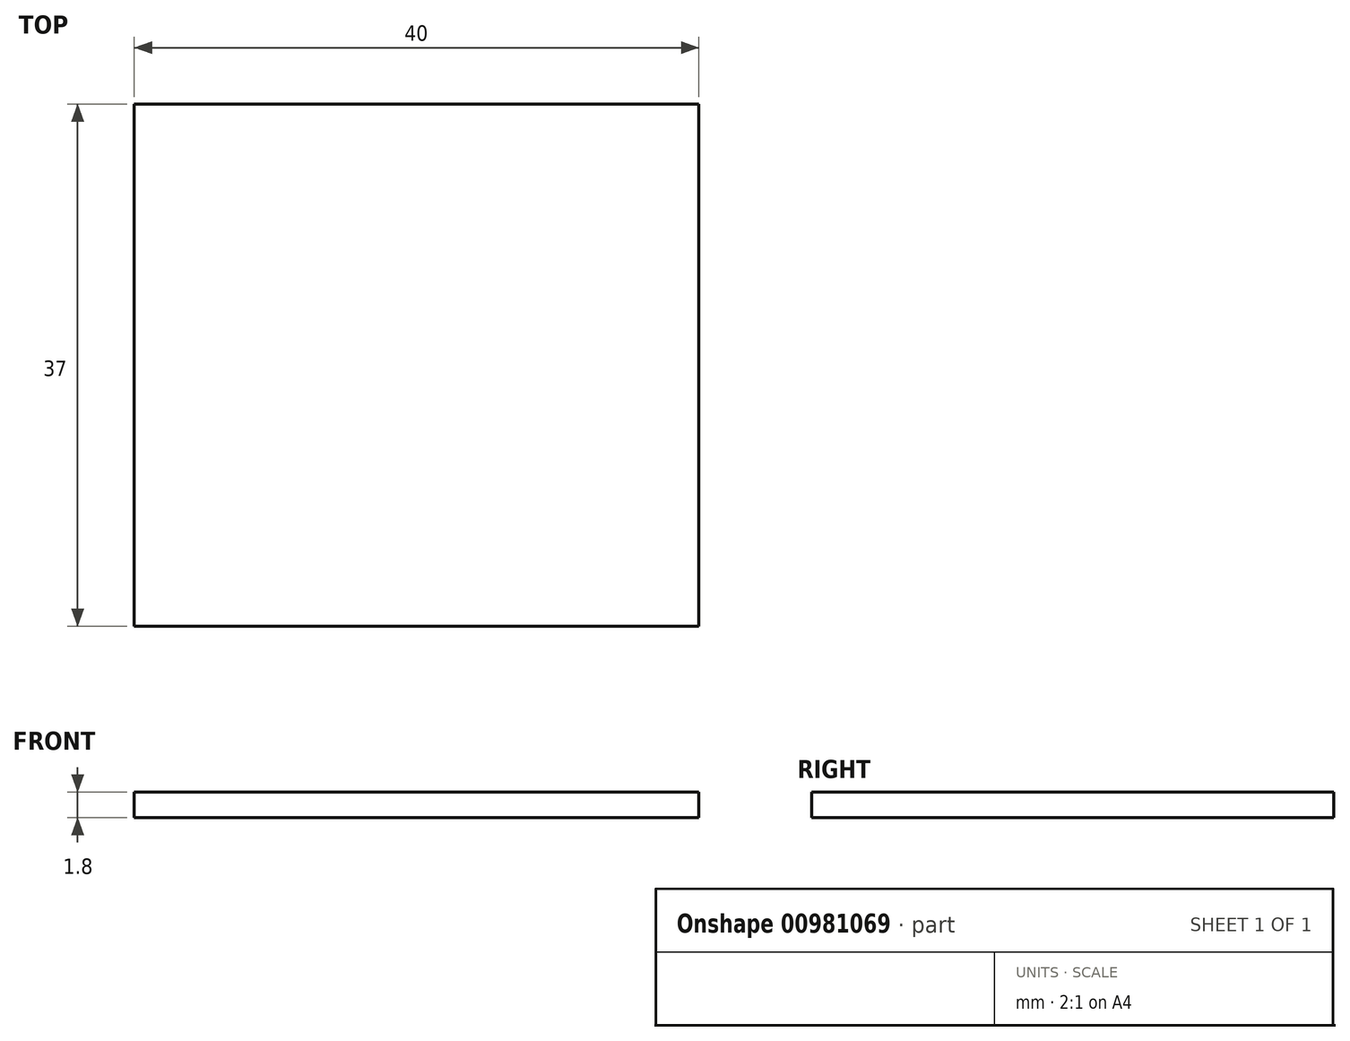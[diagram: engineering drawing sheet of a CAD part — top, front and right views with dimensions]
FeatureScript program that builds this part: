
annotation { "Feature Type Name" : "Feature", "Feature Type Description" : "" }
export const myFeature = defineFeature(function(context is Context, id is Id, definition is map)
    precondition{}
    {
        {
            var Q0;
            Q0=qCreatedBy(makeId("Top.planeOp"),FACE);
            var sketch = newSketch(context, id + "F0", { "sketchPlane" : qUnion([Q0])});
            skLineSegment(sketch, "E0.bottom", {"start": v(0, 0) * mm, "end": v(40, 0) * mm});
            skLineSegment(sketch, "E0.top", {"start": v(0, 37) * mm, "end": v(40, 37) * mm});
            skLineSegment(sketch, "E0.left", {"start": v(0, 0) * mm, "end": v(0, 37) * mm});
            skLineSegment(sketch, "E0.right", {"start": v(40, 0) * mm, "end": v(40, 37) * mm});
            skSolve(sketch);
        }
        {
            var Q0;
            Q0=makeQuery(id+"F0.imprint","IMPRINT",FACE,{"disambiguationData":[TD([[makeQuery(id+"F0.imprint","IMPRINT",EDGE,{"derivedFrom":sQuery(id+"F0.wireOp",EDGE,"E0.bottom")}),1.0]])]});
            extrude(context, id + "F1", {"entities" : qUnion([Q0]), "depth" : 1.8 * mm, "offsetDistance" : 25 * mm});
        }
    });
